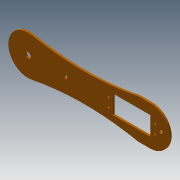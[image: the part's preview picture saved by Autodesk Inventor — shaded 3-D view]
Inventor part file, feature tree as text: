
AUTODESK INVENTOR PART (.ipt)
format: ipt  version: 2013 (Build 170138000, 138)  size: 197,120 bytes
history: native  units: mm
features: sketch x10, extrude x9
ambient origin geometry x8: Origin, YZ Plane, XZ Plane, XY Plane, X Axis, Y Axis, Z Axis, Center Point
bodies: Solid1 (feature_tree)
feature tree (19):
  extrude  "Extrusion1"  Depth=42.0mm
  sketch  "Sketch2"  dims[d8=2.0mm d9=0.0mm d27=10.5mm]
  extrude  "Extrusion2"  Depth=10.5mm
  extrude  "Extrusion3"  Depth=6.0mm
  extrude  "Extrusion4"  Depth=6.0mm
  extrude  "Extrusion5"  Depth=4.0mm
  extrude  "Extrusion6"  Depth=2.0mm TaperAngle=0.0deg
  extrude  "Extrusion7"  Depth=6.0mm
  extrude  "Extrusion8"  Depth=6.0mm
  extrude  "Extrusion9"  Depth=2.0mm TaperAngle=0.0deg
  sketch  "Sketch1"  dims[d3=42.0mm d5=42.0mm]
  sketch  "Sketch3"  dims[d28=2.0mm d29=0.0mm d30=6.0mm]
  sketch  "Sketch4"  dims[d31=10.5mm d32=6.0mm]
  sketch  "Sketch5"  dims[d33=40.0mm d34=4.0mm]
  sketch  "Sketch6"  dims[d35=2.0mm d36=0.0mm d37=2.0mm d38=0.0mm]
  sketch  "Sketch7"  dims[d39=40.0mm d40=6.0mm]
  sketch  "Sketch8"  dims[d41=2.0mm d42=0.0mm d43=6.0mm]
  sketch  "Sketch9"  dims[d44=2.0mm d45=0.0mm d46=2.0mm d47=0.0mm]
  sketch  "Sketch10"  dims[d48=10.5mm d49=18.1mm d50=55.0mm d51=27.5mm d52=20.0mm d53=40.2mm d54=3.7mm d56=2.65mm d57=2.65mm d58=3.0mm d59=3.0mm d60=2.65mm d61=2.65mm d62=3.0mm d63=3.0mm d64=2.0mm d65=0.0mm d66=6.0mm d67=40.0mm d69=10.0mm d71=4.0mm d72=4.0mm d73=2.0mm d74=0.0mm]
